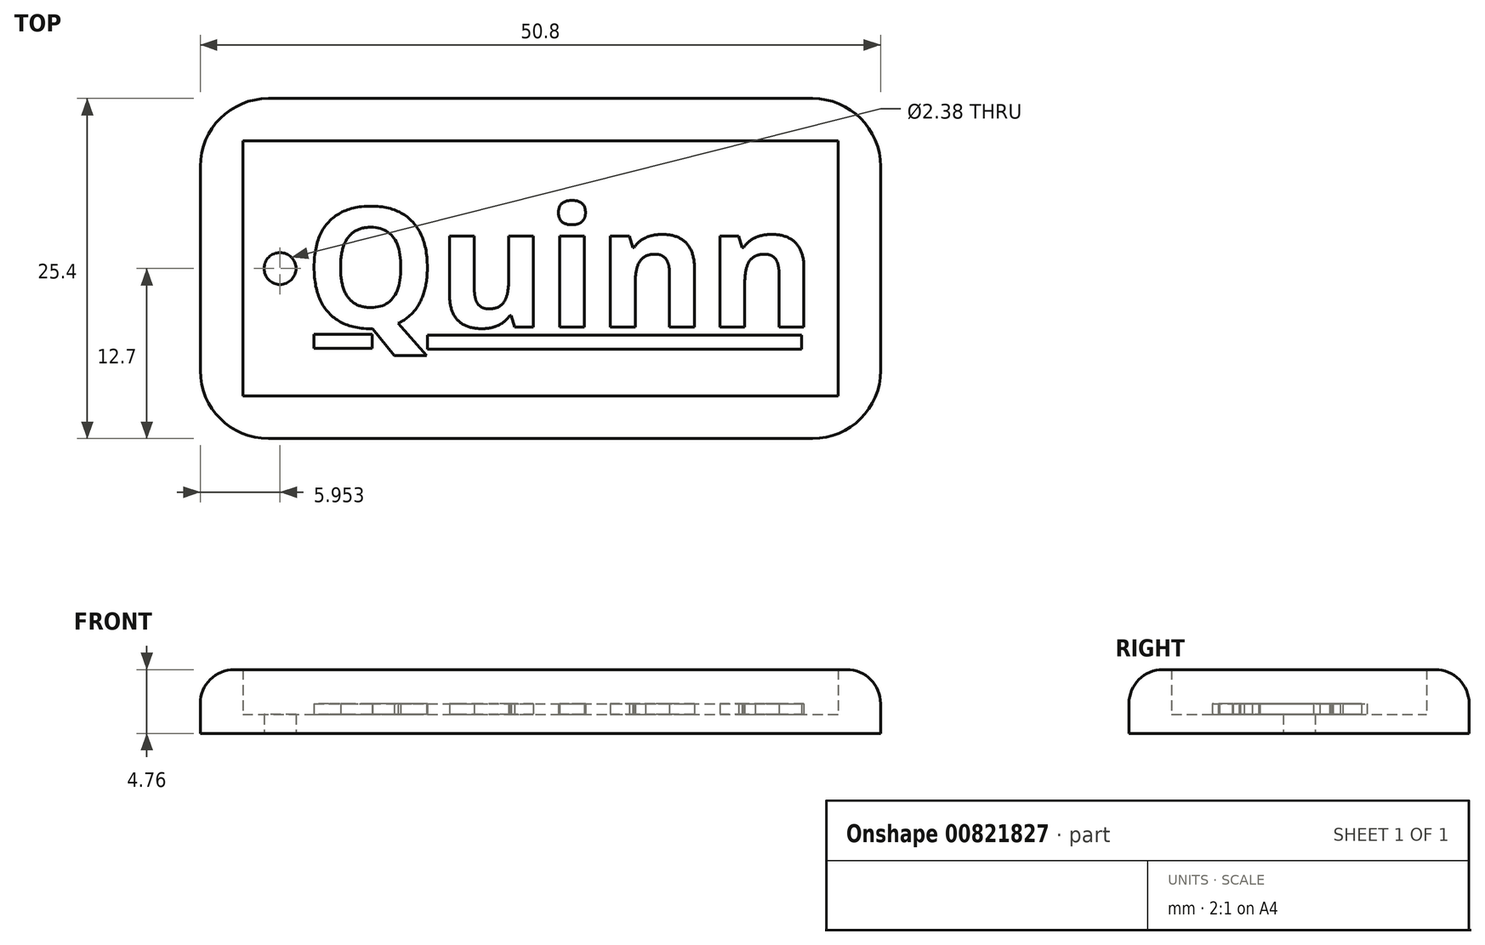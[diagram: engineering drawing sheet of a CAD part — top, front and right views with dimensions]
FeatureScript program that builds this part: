
annotation { "Feature Type Name" : "Feature", "Feature Type Description" : "" }
export const myFeature = defineFeature(function(context is Context, id is Id, definition is map)
    precondition{}
    {
        {
            var Q0;
            Q0=qCreatedBy(makeId("Top.planeOp"),FACE);
            var sketch = newSketch(context, id + "F0", { "sketchPlane" : qUnion([Q0])});
            skLineSegment(sketch, "E0", {"start": v(0, 0) * mm, "end": v(50.8, 0) * mm});
            skLineSegment(sketch, "E1", {"start": v(50.8, 0) * mm, "end": v(50.8, 25.4) * mm});
            skLineSegment(sketch, "E2", {"start": v(50.8, 25.4) * mm, "end": v(0, 25.4) * mm});
            skLineSegment(sketch, "E3", {"start": v(0, 25.4) * mm, "end": v(0, 0) * mm});
            skCircle(sketch, "E4", {"center": v(5.95, 12.7) * mm, "radius": 1.2 * mm});
            skPoint(sketch, "E4.centerSnap0", {"position": v(0, 12.7) * mm});
            skLineSegment(sketch, "E5.0", {"start": v(47.62, 22.23) * mm, "end": v(3.18, 22.22) * mm});
            skLineSegment(sketch, "E5.1", {"start": v(47.62, 3.18) * mm, "end": v(47.62, 22.23) * mm});
            skLineSegment(sketch, "E5.2", {"start": v(3.18, 3.18) * mm, "end": v(47.62, 3.18) * mm});
            skLineSegment(sketch, "E5.3", {"start": v(3.18, 22.22) * mm, "end": v(3.18, 3.18) * mm});
            skSolve(sketch);
        }
        {
            var Q0;
            Q0 = qSketchRegion(id + "F0", true);
            var Q1;
            Q1=makeQuery(id+"F0.imprint","IMPRINT",FACE,{"disambiguationData":[TD([[makeQuery(id+"F0.imprint","IMPRINT",EDGE,{"derivedFrom":sQuery(id+"F0.wireOp",EDGE,"E4")}),-1.0]])]});
            extrude(context, id + "F1", {"entities" : qUnion([Q0, Q1]), "depth" : 1.41 * mm, "offsetDistance" : 25.4 * mm});
        }
        {
            var Q0;
            Q0 = qSketchRegion(id + "F0", true);
            extrude(context, id + "F2", {"entities" : qUnion([Q0]), "operationType" : NewBodyOperationType.ADD, "depth" : 4.76 * mm, "offsetDistance" : 25.4 * mm});
        }
        {
            var Q0;
            {var subQ0=sQuery(id+"F0.wireOp",EDGE,"E1");var subQ1=sQuery(id+"F0.wireOp",EDGE,"E0");Q0=makeQuery(id+"F2.boolean.opBoolean","MERGE",EDGE,{"derivedFrom":[makeQuery(id+"F1.opExtrude","SWEPT_EDGE",EDGE,{"disambiguationData":[OSD([subQ1,subQ0])]}),makeQuery(id+"F2.opExtrude","SWEPT_EDGE",EDGE,{"disambiguationData":[OSD([subQ1,subQ0])]})]});}
            var Q1;
            {var subQ0=sQuery(id+"F0.wireOp",EDGE,"E2");var subQ1=sQuery(id+"F0.wireOp",EDGE,"E1");Q1=makeQuery(id+"F2.boolean.opBoolean","MERGE",EDGE,{"derivedFrom":[makeQuery(id+"F1.opExtrude","SWEPT_EDGE",EDGE,{"disambiguationData":[OSD([subQ1,subQ0])]}),makeQuery(id+"F2.opExtrude","SWEPT_EDGE",EDGE,{"disambiguationData":[OSD([subQ1,subQ0])]})]});}
            var Q2;
            {var subQ0=sQuery(id+"F0.wireOp",EDGE,"E3");var subQ1=sQuery(id+"F0.wireOp",EDGE,"E2");Q2=makeQuery(id+"F2.boolean.opBoolean","MERGE",EDGE,{"derivedFrom":[makeQuery(id+"F1.opExtrude","SWEPT_EDGE",EDGE,{"disambiguationData":[OSD([subQ1,subQ0])]}),makeQuery(id+"F2.opExtrude","SWEPT_EDGE",EDGE,{"disambiguationData":[OSD([subQ1,subQ0])]})]});}
            var Q3;
            {var subQ0=sQuery(id+"F0.wireOp",EDGE,"E3");var subQ1=sQuery(id+"F0.wireOp",EDGE,"E0");Q3=makeQuery(id+"F2.boolean.opBoolean","MERGE",EDGE,{"derivedFrom":[makeQuery(id+"F1.opExtrude","SWEPT_EDGE",EDGE,{"disambiguationData":[OSD([subQ1,subQ0])]}),makeQuery(id+"F2.opExtrude","SWEPT_EDGE",EDGE,{"disambiguationData":[OSD([subQ1,subQ0])]})]});}
            fillet(context, id + "F3", {"entities" : qUnion([Q0, Q1, Q2, Q3]), "radius" : 5.08 * mm, "tangentPropagation" : true, "allowEdgeOverflow" : false});
        }
        {
            var Q0;
            Q0=makeQuery(id+"F2.opExtrude","CAP_EDGE",EDGE,{"disambiguationData":[OSD([sQuery(id+"F0.wireOp",EDGE,"E0")])],"isStart":false});
            fillet(context, id + "F4", {"entities" : qUnion([Q0]), "radius" : 2.54 * mm, "tangentPropagation" : true, "allowEdgeOverflow" : false});
        }
        {
            var Q0;
            Q0=makeQuery(id+"F1.opExtrude","CAP_FACE",FACE,{"disambiguationData":[OSD([sQuery(id+"F0.wireOp",EDGE,"E0"),sQuery(id+"F0.wireOp",EDGE,"E1"),sQuery(id+"F0.wireOp",EDGE,"E2"),sQuery(id+"F0.wireOp",EDGE,"E3"),sQuery(id+"F0.wireOp",EDGE,"E4")])],"isStart":false});
            var sketch = newSketch(context, id + "F5", { "sketchPlane" : qUnion([Q0])});
            skText(sketch, "E6", { "text": "Quinn", "fontName": "OpenSans-Bold.ttf"});
            skLineSegment(sketch, "E7.bottom", {"start": v(8.5, 7.78) * mm, "end": v(12.83, 7.78) * mm});
            skLineSegment(sketch, "E7.top", {"start": v(8.5, 6.75) * mm, "end": v(12.83, 6.75) * mm});
            skLineSegment(sketch, "E7.left", {"start": v(8.5, 7.78) * mm, "end": v(8.5, 6.75) * mm});
            skLineSegment(sketch, "E7.right", {"start": v(12.83, 7.78) * mm, "end": v(12.83, 6.75) * mm});
            skLineSegment(sketch, "E8.bottom", {"start": v(16.96, 7.71) * mm, "end": v(44.9, 7.71) * mm});
            skLineSegment(sketch, "E8.top", {"start": v(16.96, 6.68) * mm, "end": v(44.9, 6.68) * mm});
            skLineSegment(sketch, "E8.left", {"start": v(16.96, 7.71) * mm, "end": v(16.96, 6.68) * mm});
            skLineSegment(sketch, "E8.right", {"start": v(44.9, 7.71) * mm, "end": v(44.9, 6.68) * mm});
            const initialGuessF5  = {"E6": [0.00777, 0.00833, 1, 0, 0.00896]};
            skSetInitialGuess(sketch, initialGuessF5);
            skSolve(sketch);
        }
        {
            var Q0;
            Q0 = qSketchRegion(id + "F5", true);
            extrude(context, id + "F6", {"entities" : qUnion([Q0]), "operationType" : NewBodyOperationType.ADD, "depth" : 0.8 * mm, "offsetDistance" : 25.4 * mm});
        }
    });
